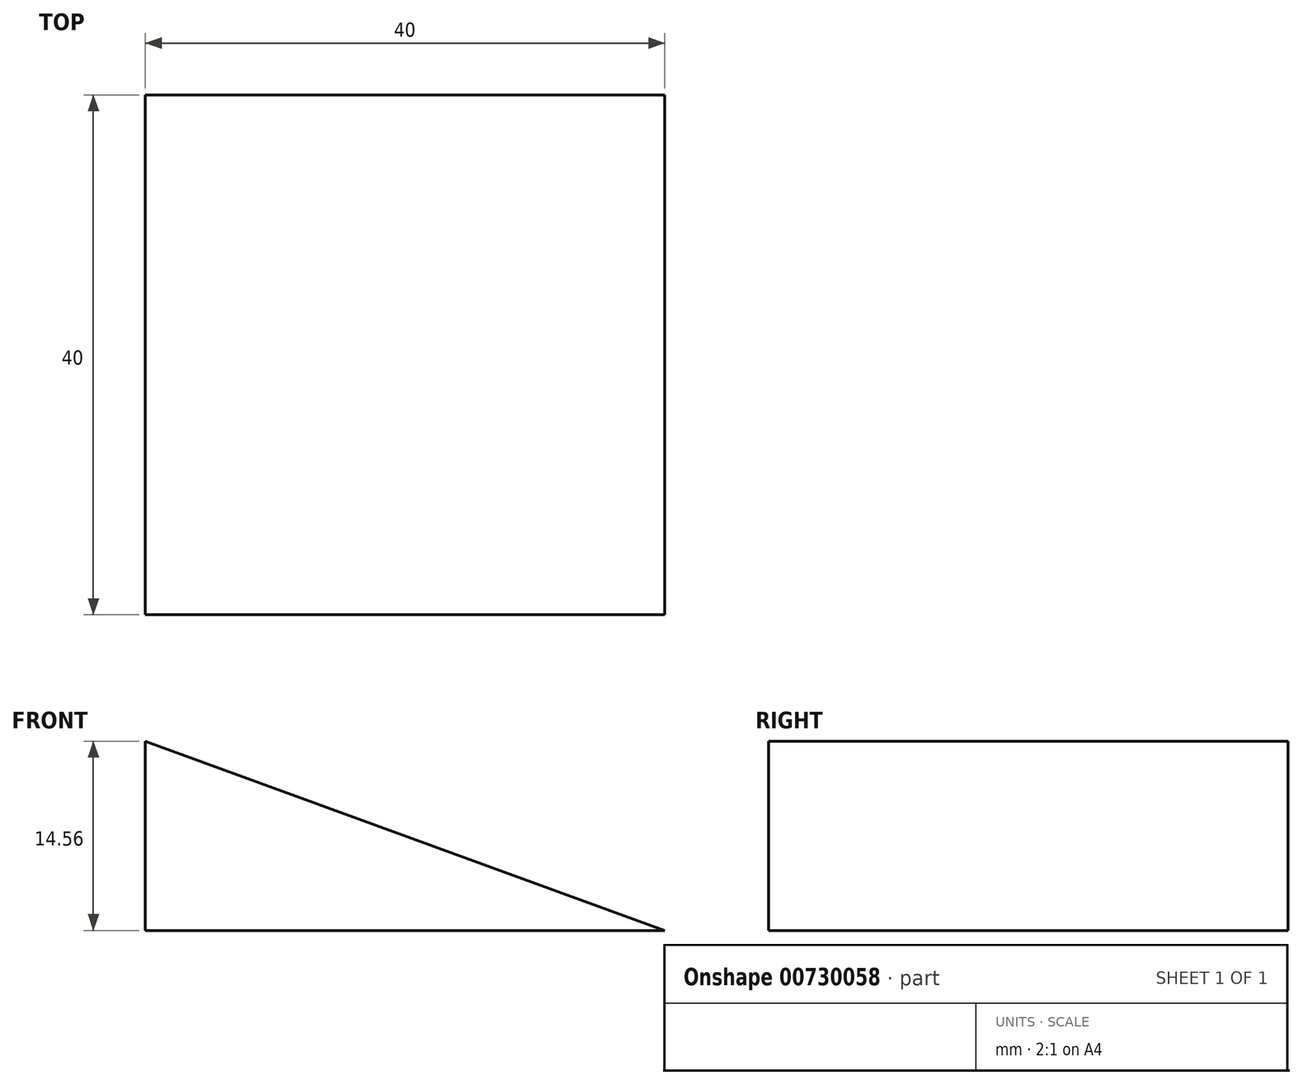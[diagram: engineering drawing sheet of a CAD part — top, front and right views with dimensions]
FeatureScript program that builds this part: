
annotation { "Feature Type Name" : "Feature", "Feature Type Description" : "" }
export const myFeature = defineFeature(function(context is Context, id is Id, definition is map)
    precondition{}
    {
        {
            var Q0;
            Q0=qCreatedBy(makeId("Front.planeOp"),FACE);
            var sketch = newSketch(context, id + "F0", { "sketchPlane" : qUnion([Q0])});
            skLineSegment(sketch, "E0", {"start": v(0, 0) * mm, "end": v(0, 14.56) * mm});
            skLineSegment(sketch, "E1", {"start": v(0, 14.56) * mm, "end": v(40, 0) * mm});
            skLineSegment(sketch, "E2", {"start": v(40, 0) * mm, "end": v(0, 0) * mm});
            skSolve(sketch);
        }
        {
            var Q0;
            Q0=makeQuery(id+"F0.imprint","IMPRINT",FACE,{"disambiguationData":[TD([[makeQuery(id+"F0.imprint","IMPRINT",EDGE,{"derivedFrom":sQuery(id+"F0.wireOp",EDGE,"E0")}),-1.0]])]});
            extrude(context, id + "F1", {"entities" : qUnion([Q0]), "depth" : 40 * mm, "offsetDistance" : 25 * mm});
        }
    });
